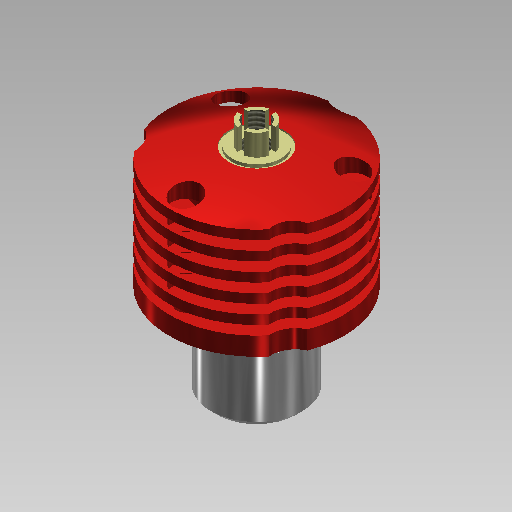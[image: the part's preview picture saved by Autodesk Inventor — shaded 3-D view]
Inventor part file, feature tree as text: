
AUTODESK INVENTOR PART (.ipt)
format: ipt  version: 2018.1 (Build 221171000, 171)  size: 440,832 bytes
history: native  units: in
note: dims shown in document units (in); Inventor stores cm internally (conversion verified against a paired STEP export)
features: sketch x13, extrude x11, revolve x2, plane x2, thread x1, chamfer x1
ambient origin geometry x8: Origin, YZ Plane, XZ Plane, XY Plane, X Axis, Y Axis, Z Axis, Center Point
bodies: Solid1 (feature_tree)
feature tree (30):
  revolve  "Revolution1"  [1 undecoded]
  extrude  "Extrusion1"  Depth=0.7874in
  plane  "Work Plane1"
  sketch  "Sketch3"  dims[d27=0.0in d28=90.0deg]
  revolve  "Revolution2"  Angle=90.0deg
  extrude  "Extrusion2"  Depth=0.1969in TaperAngle=0.0deg
  extrude  "Extrusion3"  Depth=0.0197in TaperAngle=0.0deg
  extrude  "Extrusion4"  Depth=0.0197in TaperAngle=0.0deg
  extrude  "Extrusion5"  Depth=0.4724in TaperAngle=0.0deg
  extrude  "Extrusion6"  Depth=0.3937in TaperAngle=0.0deg
  extrude  "Extrusion8"  Depth=0.0591in TaperAngle=0.0deg
  extrude  "Extrusion9"  Depth=0.0591in TaperAngle=45.0deg
  thread  "Thread1"  [1 undecoded]
  extrude  "Extrusion10"  [1 undecoded]
  plane  "Work Plane2"
  extrude  "Extrusion11"  [1 undecoded]
  extrude  "Extrusion12"  [1 undecoded]
  chamfer  "Chamfer1"  [1 undecoded]
  sketch  "Sketch1"  dims[d7=90.0deg d8=0.5118in]
  sketch  "Sketch2"  dims[d9=0.9449in d10=0.0in d11=0.7874in]
  sketch  "Sketch4"  dims[d29=0.6299in d30=0.0in d34=0.1969in d35=0.0in]
  sketch  "Sketch5"  dims[d39=0.9843in d40=0.0in d42=0.0197in d43=0.0in]
  sketch  "Sketch6"  dims[d44=0.315in d45=0.0197in d46=0.0in]
  sketch  "Sketch7"  dims[d55=0.1378in d56=0.0in d58=0.4724in d59=0.0in]
  sketch  "Sketch8"  dims[d60=0.3937in d61=0.0in d66=0.1378in d67=0.0in]
  sketch  "Sketch9"  dims[d68=-0.0591in d78=0.0591in d79=0.0in]
  sketch  "Sketch10"  dims[d81=0.0591in d82=0.0in d83=0.0394in d84=0.0787in d85=45.0deg]
  sketch  "Sketch11"
  sketch  "Sketch12"
  sketch  "Sketch13"
note: 6 required parameter values undecoded (feature->parameter linkage not recoverable at this tier; creation-order binding heuristic only, values carry confidence <= 0.55)